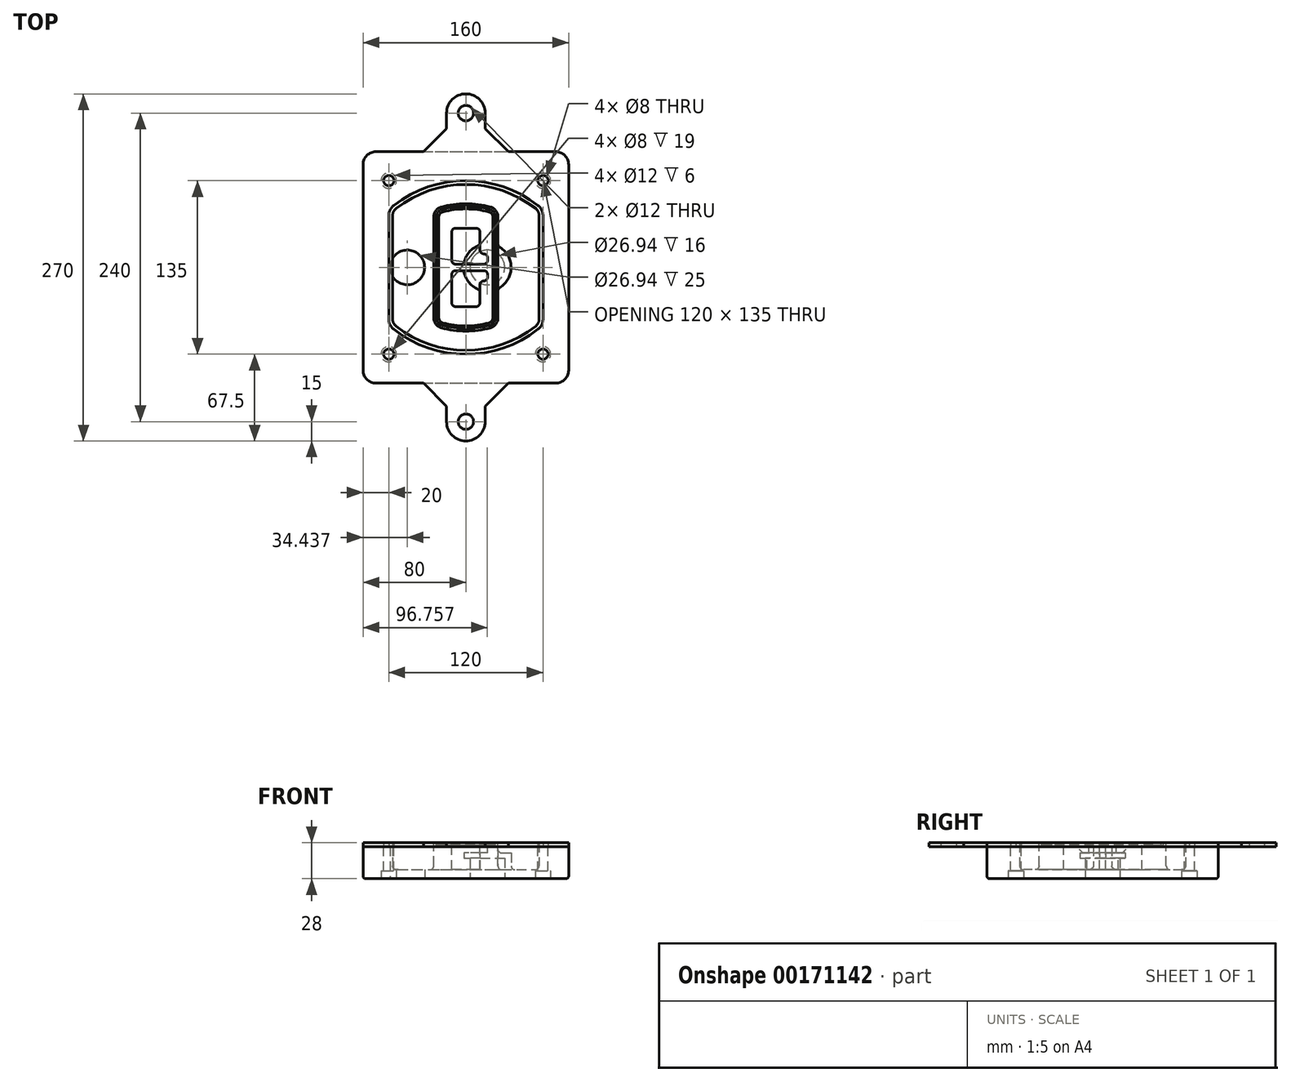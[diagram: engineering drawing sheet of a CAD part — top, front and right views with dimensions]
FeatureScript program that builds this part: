
annotation { "Feature Type Name" : "Feature", "Feature Type Description" : "" }
export const myFeature = defineFeature(function(context is Context, id is Id, definition is map)
    precondition{}
    {
        {
            var Q0;
            Q0=qCreatedBy(makeId("Top.planeOp"),FACE);
            var sketch = newSketch(context, id + "F0", { "sketchPlane" : qUnion([Q0])});
            skPoint(sketch, "E0.rect.middle", {"position": v(0, 0) * mm});
            skLineSegment(sketch, "E1.bottom", {"start": v(-70, -90) * mm, "end": v(70, -90) * mm});
            skLineSegment(sketch, "E1.top", {"start": v(-70, 90) * mm, "end": v(70, 90) * mm});
            skLineSegment(sketch, "E1.left", {"start": v(-80, -80) * mm, "end": v(-80, 80) * mm});
            skLineSegment(sketch, "E1.right", {"start": v(80, -80) * mm, "end": v(80, 80) * mm});
            skLineSegment(sketch, "E2", {"start": v(-80, 90) * mm, "end": v(80, -90) * mm, "construction": true});
            skLineSegment(sketch, "E3", {"start": v(80, 90) * mm, "end": v(-80, -90) * mm, "construction": true});
            skCircle(sketch, "E4", {"center": v(-60, 67.5) * mm, "radius": 4 * mm});
            skCircle(sketch, "E5", {"center": v(60, 67.5) * mm, "radius": 4 * mm});
            skCircle(sketch, "E6", {"center": v(60, -67.5) * mm, "radius": 4 * mm});
            skCircle(sketch, "E7", {"center": v(-60, -67.5) * mm, "radius": 4 * mm});
            skLineSegment(sketch, "E8", {"start": v(-60, 67.5) * mm, "end": v(60, 67.5) * mm, "construction": true});
            skLineSegment(sketch, "E9", {"start": v(60, 67.5) * mm, "end": v(60, -67.5) * mm, "construction": true});
            skLineSegment(sketch, "E10", {"start": v(60, -67.5) * mm, "end": v(-60, -67.5) * mm, "construction": true});
            skLineSegment(sketch, "E11", {"start": v(-60, -67.5) * mm, "end": v(-60, 67.5) * mm, "construction": true});
            skLineSegment(sketch, "E12", {"start": v(-60, 40.3) * mm, "end": v(-60, -40.3) * mm});
            skLineSegment(sketch, "E13", {"start": v(60, 40.3) * mm, "end": v(60, -40.3) * mm});
            skArc(sketch, "E14", {"start": v(56.15, 48.18) * mm, "mid": v(0, 67.5) * mm, "end": v(-56.15, 48.18) * mm});
            skArc(sketch, "E15", {"start": v(-56.15, -48.18) * mm, "mid": v(0, -67.5) * mm, "end": v(56.15, -48.18) * mm});
            skLineSegment(sketch, "E16", {"start": v(-60, 0) * mm, "end": v(60, 0) * mm, "construction": true});
            skPoint(sketch, "E17.visualSharp", {"position": v(-60, -45) * mm});
            skArc(sketch, "E17.filletArc", {"start": v(-60, -40.3) * mm, "mid": v(-58.99, -44.68) * mm, "end": v(-56.15, -48.18) * mm});
            skPoint(sketch, "E18.visualSharp", {"position": v(-60, 45) * mm});
            skArc(sketch, "E18.filletArc", {"start": v(-56.15, 48.18) * mm, "mid": v(-58.99, 44.68) * mm, "end": v(-60, 40.3) * mm});
            skPoint(sketch, "E19.visualSharp", {"position": v(60, 45) * mm});
            skArc(sketch, "E19.filletArc", {"start": v(60, 40.3) * mm, "mid": v(58.99, 44.68) * mm, "end": v(56.15, 48.18) * mm});
            skPoint(sketch, "E20.visualSharp", {"position": v(60, -45) * mm});
            skArc(sketch, "E20.filletArc", {"start": v(56.15, -48.18) * mm, "mid": v(58.99, -44.68) * mm, "end": v(60, -40.3) * mm});
            skPoint(sketch, "E21.visualSharp", {"position": v(-80, 90) * mm});
            skArc(sketch, "E21.filletArc", {"start": v(-70, 90) * mm, "mid": v(-77.07, 87.07) * mm, "end": v(-80, 80) * mm});
            skPoint(sketch, "E22.visualSharp", {"position": v(80, 90) * mm});
            skArc(sketch, "E22.filletArc", {"start": v(80, 80) * mm, "mid": v(77.07, 87.07) * mm, "end": v(70, 90) * mm});
            skPoint(sketch, "E23.visualSharp", {"position": v(80, -90) * mm});
            skArc(sketch, "E23.filletArc", {"start": v(70, -90) * mm, "mid": v(77.07, -87.07) * mm, "end": v(80, -80) * mm});
            skPoint(sketch, "E24.visualSharp", {"position": v(-80, -90) * mm});
            skArc(sketch, "E24.filletArc", {"start": v(-80, -80) * mm, "mid": v(-77.07, -87.07) * mm, "end": v(-70, -90) * mm});
            skArc(sketch, "E25.0", {"start": v(57, 40.3) * mm, "mid": v(56.3, 43.36) * mm, "end": v(54.3, 45.81) * mm});
            skLineSegment(sketch, "E25.1", {"start": v(57, 40.3) * mm, "end": v(57, -40.3) * mm});
            skArc(sketch, "E25.2", {"start": v(54.3, -45.81) * mm, "mid": v(56.3, -43.36) * mm, "end": v(57, -40.3) * mm});
            skArc(sketch, "E25.3", {"start": v(-54.3, -45.81) * mm, "mid": v(0, -64.5) * mm, "end": v(54.3, -45.81) * mm});
            skArc(sketch, "E25.4", {"start": v(-57, -40.3) * mm, "mid": v(-56.3, -43.36) * mm, "end": v(-54.3, -45.81) * mm});
            skArc(sketch, "E25.5", {"start": v(54.3, 45.81) * mm, "mid": v(0, 64.5) * mm, "end": v(-54.3, 45.81) * mm});
            skLineSegment(sketch, "E25.6", {"start": v(-57, 40.3) * mm, "end": v(-57, -40.3) * mm});
            skArc(sketch, "E25.7", {"start": v(-54.3, 45.81) * mm, "mid": v(-56.3, 43.36) * mm, "end": v(-57, 40.3) * mm});
            skArc(sketch, "E26.0", {"start": v(-58.62, 51.33) * mm, "mid": v(-62.58, 46.43) * mm, "end": v(-64, 40.3) * mm});
            skArc(sketch, "E26.1", {"start": v(58.62, 51.33) * mm, "mid": v(0, 71.5) * mm, "end": v(-58.62, 51.33) * mm});
            skArc(sketch, "E26.2", {"start": v(64, 40.3) * mm, "mid": v(62.58, 46.43) * mm, "end": v(58.62, 51.33) * mm});
            skLineSegment(sketch, "E26.3", {"start": v(64, 40.3) * mm, "end": v(64, -40.3) * mm});
            skArc(sketch, "E26.4", {"start": v(58.62, -51.33) * mm, "mid": v(62.58, -46.43) * mm, "end": v(64, -40.3) * mm});
            skLineSegment(sketch, "E26.5", {"start": v(-64, 40.3) * mm, "end": v(-64, -40.3) * mm});
            skArc(sketch, "E26.6", {"start": v(-58.62, -51.33) * mm, "mid": v(0, -71.5) * mm, "end": v(58.62, -51.33) * mm});
            skArc(sketch, "E26.7", {"start": v(-64, -40.3) * mm, "mid": v(-62.58, -46.43) * mm, "end": v(-58.62, -51.33) * mm});
            skSolve(sketch);
        }
        {
            var Q0;
            Q0=makeQuery(id+"F0.imprint","IMPRINT",FACE,{"disambiguationData":[TD([[makeQuery(id+"F0.imprint","IMPRINT",EDGE,{"derivedFrom":sQuery(id+"F0.wireOp",EDGE,"E1.bottom")}),1.0]])]});
            var Q1;
            Q1=makeQuery(id+"F0.imprint","IMPRINT",FACE,{"disambiguationData":[TD([[makeQuery(id+"F0.imprint","IMPRINT",EDGE,{"derivedFrom":sQuery(id+"F0.wireOp",EDGE,"E12")}),1.0]])]});
            var Q2;
            Q2=makeQuery(id+"F0.imprint","IMPRINT",FACE,{"disambiguationData":[TD([[makeQuery(id+"F0.imprint","IMPRINT",EDGE,{"derivedFrom":sQuery(id+"F0.wireOp",EDGE,"E25.0")}),1.0]])]});
            var Q3;
            Q3=makeQuery(id+"F0.imprint","IMPRINT",FACE,{"disambiguationData":[TD([[makeQuery(id+"F0.imprint","IMPRINT",EDGE,{"derivedFrom":sQuery(id+"F0.wireOp",EDGE,"E12")}),-1.0]])]});
            extrude(context, id + "F1", {"entities" : qUnion([Q0, Q1, Q2, Q3]), "oppositeDirection" : true, "depth" : 25 * mm});
        }
        {
            var Q0;
            Q0=makeQuery(id+"F0.imprint","IMPRINT",FACE,{"disambiguationData":[TD([[makeQuery(id+"F0.imprint","IMPRINT",EDGE,{"derivedFrom":sQuery(id+"F0.wireOp",EDGE,"E12")}),1.0]])]});
            extrude(context, id + "F2", {"entities" : qUnion([Q0]), "operationType" : NewBodyOperationType.ADD, "depth" : 3 * mm});
        }
        {
            var Q0;
            Q0=makeQuery(id+"F0.imprint","IMPRINT",FACE,{"disambiguationData":[TD([[makeQuery(id+"F0.imprint","IMPRINT",EDGE,{"derivedFrom":sQuery(id+"F0.wireOp",EDGE,"E25.0")}),1.0]])]});
            extrude(context, id + "F3", {"entities" : qUnion([Q0]), "operationType" : NewBodyOperationType.REMOVE, "oppositeDirection" : true, "depth" : 18 * mm});
        }
        {
            var Q0;
            Q0=makeQuery(id+"F2.opExtrude","CAP_FACE",FACE,{"disambiguationData":[OSD([sQuery(id+"F0.wireOp",EDGE,"E12"),sQuery(id+"F0.wireOp",EDGE,"E13"),sQuery(id+"F0.wireOp",EDGE,"E14"),sQuery(id+"F0.wireOp",EDGE,"E15"),sQuery(id+"F0.wireOp",EDGE,"E17.filletArc"),sQuery(id+"F0.wireOp",EDGE,"E18.filletArc"),sQuery(id+"F0.wireOp",EDGE,"E19.filletArc"),sQuery(id+"F0.wireOp",EDGE,"E20.filletArc"),sQuery(id+"F0.wireOp",EDGE,"E25.0"),sQuery(id+"F0.wireOp",EDGE,"E25.1"),sQuery(id+"F0.wireOp",EDGE,"E25.2"),sQuery(id+"F0.wireOp",EDGE,"E25.3"),sQuery(id+"F0.wireOp",EDGE,"E25.4"),sQuery(id+"F0.wireOp",EDGE,"E25.5"),sQuery(id+"F0.wireOp",EDGE,"E25.6"),sQuery(id+"F0.wireOp",EDGE,"E25.7")])],"isStart":false});
            var sketch = newSketch(context, id + "F4", { "sketchPlane" : qUnion([Q0])});
            skArc(sketch, "E27.0", {"start": v(-19.08, -46.97) * mm, "mid": v(0, -49.5) * mm, "end": v(19.08, -46.97) * mm});
            skArc(sketch, "E28.0", {"start": v(19.08, 46.97) * mm, "mid": v(0, 49.5) * mm, "end": v(-19.08, 46.97) * mm});
            skLineSegment(sketch, "E29", {"start": v(-25, 39.25) * mm, "end": v(-25, -39.25) * mm});
            skLineSegment(sketch, "E30", {"start": v(25, 39.25) * mm, "end": v(25, -39.25) * mm});
            skLineSegment(sketch, "E31", {"start": v(-25, 45.1) * mm, "end": v(25, 45.1) * mm, "construction": true});
            skLineSegment(sketch, "E32", {"start": v(-25, -45.1) * mm, "end": v(25, -45.1) * mm, "construction": true});
            skPoint(sketch, "E33.visualSharp", {"position": v(-25, 45.1) * mm});
            skArc(sketch, "E33.filletArc", {"start": v(-19.08, 46.97) * mm, "mid": v(-23.35, 44.11) * mm, "end": v(-25, 39.25) * mm});
            skPoint(sketch, "E34.visualSharp", {"position": v(25, 45.1) * mm});
            skArc(sketch, "E34.filletArc", {"start": v(25, 39.25) * mm, "mid": v(23.35, 44.11) * mm, "end": v(19.08, 46.97) * mm});
            skPoint(sketch, "E35.visualSharp", {"position": v(25, -45.1) * mm});
            skArc(sketch, "E35.filletArc", {"start": v(19.08, -46.97) * mm, "mid": v(23.35, -44.11) * mm, "end": v(25, -39.25) * mm});
            skPoint(sketch, "E36.visualSharp", {"position": v(-25, -45.1) * mm});
            skArc(sketch, "E36.filletArc", {"start": v(-25, -39.25) * mm, "mid": v(-23.35, -44.11) * mm, "end": v(-19.08, -46.97) * mm});
            skArc(sketch, "E37.0", {"start": v(54.3, 45.81) * mm, "mid": v(0, 64.5) * mm, "end": v(-54.3, 45.81) * mm});
            skArc(sketch, "E37.1", {"start": v(-54.3, 45.81) * mm, "mid": v(-56.3, 43.36) * mm, "end": v(-57, 40.3) * mm});
            skLineSegment(sketch, "E37.2", {"start": v(-57, 40.3) * mm, "end": v(-57, -40.3) * mm});
            skArc(sketch, "E37.3", {"start": v(-57, -40.3) * mm, "mid": v(-56.3, -43.36) * mm, "end": v(-54.3, -45.81) * mm});
            skArc(sketch, "E37.4", {"start": v(-54.3, -45.81) * mm, "mid": v(0, -64.5) * mm, "end": v(54.3, -45.81) * mm});
            skArc(sketch, "E37.5", {"start": v(54.3, -45.81) * mm, "mid": v(56.3, -43.36) * mm, "end": v(57, -40.3) * mm});
            skLineSegment(sketch, "E37.6", {"start": v(57, 40.3) * mm, "end": v(57, -40.3) * mm});
            skArc(sketch, "E37.7", {"start": v(57, 40.3) * mm, "mid": v(56.3, 43.36) * mm, "end": v(54.3, 45.81) * mm});
            skLineSegment(sketch, "E38.0", {"start": v(23, 39.25) * mm, "end": v(23, -39.25) * mm});
            skArc(sketch, "E38.1", {"start": v(18.56, -45.04) * mm, "mid": v(21.76, -42.9) * mm, "end": v(23, -39.25) * mm});
            skArc(sketch, "E38.2", {"start": v(-18.56, -45.04) * mm, "mid": v(0, -47.5) * mm, "end": v(18.56, -45.04) * mm});
            skArc(sketch, "E38.3", {"start": v(-23, -39.25) * mm, "mid": v(-21.76, -42.9) * mm, "end": v(-18.56, -45.04) * mm});
            skLineSegment(sketch, "E38.4", {"start": v(-23, 39.25) * mm, "end": v(-23, -39.25) * mm});
            skArc(sketch, "E38.5", {"start": v(23, 39.25) * mm, "mid": v(21.76, 42.9) * mm, "end": v(18.56, 45.04) * mm});
            skArc(sketch, "E38.6", {"start": v(-18.56, 45.04) * mm, "mid": v(-21.76, 42.9) * mm, "end": v(-23, 39.25) * mm});
            skArc(sketch, "E38.7", {"start": v(18.56, 45.04) * mm, "mid": v(0, 47.5) * mm, "end": v(-18.56, 45.04) * mm});
            skArc(sketch, "E39.0", {"start": v(21, 39.25) * mm, "mid": v(20.18, 41.68) * mm, "end": v(18.04, 43.1) * mm});
            skLineSegment(sketch, "E39.1", {"start": v(21, 39.25) * mm, "end": v(21, -39.25) * mm});
            skArc(sketch, "E39.2", {"start": v(18.04, -43.1) * mm, "mid": v(20.18, -41.68) * mm, "end": v(21, -39.25) * mm});
            skArc(sketch, "E39.3", {"start": v(-18.04, -43.1) * mm, "mid": v(0, -45.5) * mm, "end": v(18.04, -43.1) * mm});
            skArc(sketch, "E39.4", {"start": v(-21, -39.25) * mm, "mid": v(-20.18, -41.68) * mm, "end": v(-18.04, -43.1) * mm});
            skArc(sketch, "E39.5", {"start": v(18.04, 43.1) * mm, "mid": v(0, 45.5) * mm, "end": v(-18.04, 43.1) * mm});
            skLineSegment(sketch, "E39.6", {"start": v(-21, 39.25) * mm, "end": v(-21, -39.25) * mm});
            skArc(sketch, "E39.7", {"start": v(-18.04, 43.1) * mm, "mid": v(-20.18, 41.68) * mm, "end": v(-21, 39.25) * mm});
            skLineSegment(sketch, "E40", {"start": v(-25, 0) * mm, "end": v(25, 0) * mm, "construction": true});
            skLineSegment(sketch, "E41", {"start": v(-11, 5.5) * mm, "end": v(-11, 27.5) * mm});
            skLineSegment(sketch, "E42", {"start": v(-8, 30.5) * mm, "end": v(8, 30.5) * mm});
            skLineSegment(sketch, "E43", {"start": v(11, 27.5) * mm, "end": v(11, 13.5) * mm});
            skLineSegment(sketch, "E44", {"start": v(14, 10.5) * mm, "end": v(14, 10.5) * mm});
            skLineSegment(sketch, "E45", {"start": v(17, 7.5) * mm, "end": v(17, 5.5) * mm});
            skLineSegment(sketch, "E46", {"start": v(14, 2.5) * mm, "end": v(-8, 2.5) * mm});
            skPoint(sketch, "E47.visualSharp", {"position": v(-11, 30.5) * mm});
            skArc(sketch, "E47.filletArc", {"start": v(-8, 30.5) * mm, "mid": v(-10.12, 29.62) * mm, "end": v(-11, 27.5) * mm});
            skPoint(sketch, "E48.visualSharp", {"position": v(11, 30.5) * mm});
            skArc(sketch, "E48.filletArc", {"start": v(11, 27.5) * mm, "mid": v(10.12, 29.62) * mm, "end": v(8, 30.5) * mm});
            skPoint(sketch, "E49.visualSharp", {"position": v(11, 10.5) * mm});
            skArc(sketch, "E49.filletArc", {"start": v(11, 13.5) * mm, "mid": v(11.88, 11.38) * mm, "end": v(14, 10.5) * mm});
            skPoint(sketch, "E50.visualSharp", {"position": v(17, 10.5) * mm});
            skArc(sketch, "E50.filletArc", {"start": v(17, 7.5) * mm, "mid": v(16.12, 9.62) * mm, "end": v(14, 10.5) * mm});
            skPoint(sketch, "E51.visualSharp", {"position": v(17, 2.5) * mm});
            skArc(sketch, "E51.filletArc", {"start": v(14, 2.5) * mm, "mid": v(16.12, 3.38) * mm, "end": v(17, 5.5) * mm});
            skPoint(sketch, "E52.visualSharp", {"position": v(-11, 2.5) * mm});
            skArc(sketch, "E52.filletArc", {"start": v(-11, 5.5) * mm, "mid": v(-10.12, 3.38) * mm, "end": v(-8, 2.5) * mm});
            skLineSegment(sketch, "E53.0.MirrorCS", {"start": v(14, -2.5) * mm, "end": v(-8, -2.5) * mm});
            skArc(sketch, "E54.0.MirrorCS", {"start": v(-11, -5.5) * mm, "mid": v(-10.12, -3.38) * mm, "end": v(-8, -2.5) * mm});
            skLineSegment(sketch, "E55.0.MirrorCS", {"start": v(-11, -5.5) * mm, "end": v(-11, -27.5) * mm});
            skArc(sketch, "E56.0.MirrorCS", {"start": v(-8, -30.5) * mm, "mid": v(-10.12, -29.62) * mm, "end": v(-11, -27.5) * mm});
            skLineSegment(sketch, "E57.0.MirrorCS", {"start": v(-8, -30.5) * mm, "end": v(8, -30.5) * mm});
            skArc(sketch, "E58.0.MirrorCS", {"start": v(11, -27.5) * mm, "mid": v(10.12, -29.62) * mm, "end": v(8, -30.5) * mm});
            skLineSegment(sketch, "E59.0.MirrorCS", {"start": v(11, -27.5) * mm, "end": v(11, -13.5) * mm});
            skArc(sketch, "E60.0.MirrorCS", {"start": v(11, -13.5) * mm, "mid": v(11.88, -11.38) * mm, "end": v(14, -10.5) * mm});
            skArc(sketch, "E61.0.MirrorCS", {"start": v(17, -7.5) * mm, "mid": v(16.12, -9.62) * mm, "end": v(14, -10.5) * mm});
            skLineSegment(sketch, "E62.0.MirrorCS", {"start": v(17, -7.5) * mm, "end": v(17, -5.5) * mm});
            skArc(sketch, "E63.0.MirrorCS", {"start": v(14, -2.5) * mm, "mid": v(16.12, -3.38) * mm, "end": v(17, -5.5) * mm});
            skSolve(sketch);
        }
        {
            var Q0;
            Q0=makeQuery(id+"F4.imprint","IMPRINT",FACE,{"disambiguationData":[TD([[makeQuery(id+"F4.imprint","IMPRINT",EDGE,{"derivedFrom":sQuery(id+"F4.wireOp",EDGE,"E27.0")}),1.0]])]});
            var Q1;
            Q1=makeQuery(id+"F4.imprint","IMPRINT",FACE,{"disambiguationData":[TD([[makeQuery(id+"F4.imprint","IMPRINT",EDGE,{"derivedFrom":sQuery(id+"F4.wireOp",EDGE,"E38.0")}),-1.0]])]});
            var Q2;
            Q2=makeQuery(id+"F4.imprint","IMPRINT",FACE,{"disambiguationData":[TD([[makeQuery(id+"F4.imprint","IMPRINT",EDGE,{"derivedFrom":sQuery(id+"F4.wireOp",EDGE,"E39.0")}),1.0]])]});
            extrude(context, id + "F5", {"entities" : qUnion([Q0, Q1, Q2]), "operationType" : NewBodyOperationType.ADD, "endBound" : BoundingType.UP_TO_NEXT, "oppositeDirection" : true, "depth" : 25 * mm});
        }
        {
            var Q0;
            Q0=makeQuery(id+"F4.imprint","IMPRINT",FACE,{"disambiguationData":[TD([[makeQuery(id+"F4.imprint","IMPRINT",EDGE,{"derivedFrom":sQuery(id+"F4.wireOp",EDGE,"E38.0")}),-1.0]])]});
            extrude(context, id + "F6", {"entities" : qUnion([Q0]), "operationType" : NewBodyOperationType.REMOVE, "oppositeDirection" : true, "depth" : 2 * mm});
        }
        {
            var Q0;
            Q0=makeQuery(id+"F1.opExtrude","CAP_FACE",FACE,{"disambiguationData":[OSD([sQuery(id+"F0.wireOp",EDGE,"E1.bottom"),sQuery(id+"F0.wireOp",EDGE,"E1.top"),sQuery(id+"F0.wireOp",EDGE,"E1.left"),sQuery(id+"F0.wireOp",EDGE,"E1.right"),sQuery(id+"F0.wireOp",EDGE,"E4"),sQuery(id+"F0.wireOp",EDGE,"E5"),sQuery(id+"F0.wireOp",EDGE,"E6"),sQuery(id+"F0.wireOp",EDGE,"E7"),sQuery(id+"F0.wireOp",EDGE,"E21.filletArc"),sQuery(id+"F0.wireOp",EDGE,"E22.filletArc"),sQuery(id+"F0.wireOp",EDGE,"E23.filletArc"),sQuery(id+"F0.wireOp",EDGE,"E24.filletArc")])],"isStart":false});
            var sketch = newSketch(context, id + "F7", { "sketchPlane" : qUnion([Q0])});
            skCircle(sketch, "E64", {"center": v(16.76, 0) * mm, "radius": 13.47 * mm});
            skCircle(sketch, "E65", {"center": v(-45.56, 0) * mm, "radius": 13.47 * mm});
            skLineSegment(sketch, "E66", {"start": v(80, 0) * mm, "end": v(-80, 0) * mm});
            skCircle(sketch, "E67", {"center": v(16.76, 0) * mm, "radius": 18.47 * mm});
            skCircle(sketch, "E68", {"center": v(60, -67.5) * mm, "radius": 6 * mm});
            skCircle(sketch, "E69", {"center": v(-60, -67.5) * mm, "radius": 6 * mm});
            skCircle(sketch, "E70", {"center": v(-60, 67.5) * mm, "radius": 6 * mm});
            skCircle(sketch, "E71", {"center": v(60, 67.5) * mm, "radius": 6 * mm});
            skSolve(sketch);
        }
        {
            var Q0;
            {var subQ1=sQuery(id+"F7.wireOp",EDGE,"E66");var subQ4=sQuery(id+"F7.wireOp",EDGE,"E64");var subQ6=makeQuery(id+"F7.imprint","INTERSECT",VERTEX,{"disambiguationData":[OD(0.0)],"derivedFrom":[subQ4,subQ1]});Q0=makeQuery(id+"F7.imprint","IMPRINT",FACE,{"disambiguationData":[TD([[makeQuery(id+"F7.imprint","IMPRINT",EDGE,{"disambiguationData":[TD([[subQ6,-1.0]])],"derivedFrom":subQ4}),-1.0]])]});}
            var Q1;
            {var subQ0=sQuery(id+"F7.wireOp",EDGE,"E66");var subQ1=sQuery(id+"F7.wireOp",EDGE,"E64");var subQ3=makeQuery(id+"F7.imprint","INTERSECT",VERTEX,{"disambiguationData":[OD(0.0)],"derivedFrom":[subQ1,subQ0]});Q1=makeQuery(id+"F7.imprint","IMPRINT",FACE,{"disambiguationData":[TD([[makeQuery(id+"F7.imprint","IMPRINT",EDGE,{"disambiguationData":[TD([[subQ3,-1.0]])],"derivedFrom":subQ1}),1.0]])]});}
            var Q2;
            {var subQ0=sQuery(id+"F7.wireOp",EDGE,"E66");var subQ1=sQuery(id+"F7.wireOp",EDGE,"E64");var subQ3=makeQuery(id+"F7.imprint","INTERSECT",VERTEX,{"disambiguationData":[OD(0.0)],"derivedFrom":[subQ1,subQ0]});Q2=makeQuery(id+"F7.imprint","IMPRINT",FACE,{"disambiguationData":[TD([[makeQuery(id+"F7.imprint","IMPRINT",EDGE,{"disambiguationData":[TD([[subQ3,1.0]])],"derivedFrom":subQ1}),1.0]])]});}
            var Q3;
            {var subQ1=sQuery(id+"F7.wireOp",EDGE,"E66");var subQ4=sQuery(id+"F7.wireOp",EDGE,"E64");var subQ6=makeQuery(id+"F7.imprint","INTERSECT",VERTEX,{"disambiguationData":[OD(0.0)],"derivedFrom":[subQ4,subQ1]});Q3=makeQuery(id+"F7.imprint","IMPRINT",FACE,{"disambiguationData":[TD([[makeQuery(id+"F7.imprint","IMPRINT",EDGE,{"disambiguationData":[TD([[subQ6,1.0]])],"derivedFrom":subQ4}),-1.0]])]});}
            extrude(context, id + "F8", {"entities" : qUnion([Q0, Q1, Q2, Q3]), "operationType" : NewBodyOperationType.ADD, "oppositeDirection" : true, "depth" : 20 * mm});
        }
        {
            var Q0;
            {var subQ0=sQuery(id+"F7.wireOp",EDGE,"E66");var subQ1=sQuery(id+"F7.wireOp",EDGE,"E64");var subQ3=makeQuery(id+"F7.imprint","INTERSECT",VERTEX,{"disambiguationData":[OD(0.0)],"derivedFrom":[subQ1,subQ0]});Q0=makeQuery(id+"F7.imprint","IMPRINT",FACE,{"disambiguationData":[TD([[makeQuery(id+"F7.imprint","IMPRINT",EDGE,{"disambiguationData":[TD([[subQ3,-1.0]])],"derivedFrom":subQ1}),1.0]])]});}
            var Q1;
            {var subQ0=sQuery(id+"F7.wireOp",EDGE,"E66");var subQ1=sQuery(id+"F7.wireOp",EDGE,"E64");var subQ3=makeQuery(id+"F7.imprint","INTERSECT",VERTEX,{"disambiguationData":[OD(0.0)],"derivedFrom":[subQ1,subQ0]});Q1=makeQuery(id+"F7.imprint","IMPRINT",FACE,{"disambiguationData":[TD([[makeQuery(id+"F7.imprint","IMPRINT",EDGE,{"disambiguationData":[TD([[subQ3,1.0]])],"derivedFrom":subQ1}),1.0]])]});}
            extrude(context, id + "F9", {"entities" : qUnion([Q0, Q1]), "operationType" : NewBodyOperationType.REMOVE, "oppositeDirection" : true, "depth" : 16 * mm});
        }
        {
            var Q0;
            {var subQ0=sQuery(id+"F7.wireOp",EDGE,"E66");var subQ1=sQuery(id+"F7.wireOp",EDGE,"E65");var subQ3=makeQuery(id+"F7.imprint","INTERSECT",VERTEX,{"disambiguationData":[OD(0.0)],"derivedFrom":[subQ1,subQ0]});Q0=makeQuery(id+"F7.imprint","IMPRINT",FACE,{"disambiguationData":[TD([[makeQuery(id+"F7.imprint","IMPRINT",EDGE,{"disambiguationData":[TD([[subQ3,-1.0]])],"derivedFrom":subQ1}),1.0]])]});}
            var Q1;
            {var subQ0=sQuery(id+"F7.wireOp",EDGE,"E66");var subQ1=sQuery(id+"F7.wireOp",EDGE,"E65");var subQ3=makeQuery(id+"F7.imprint","INTERSECT",VERTEX,{"disambiguationData":[OD(0.0)],"derivedFrom":[subQ1,subQ0]});Q1=makeQuery(id+"F7.imprint","IMPRINT",FACE,{"disambiguationData":[TD([[makeQuery(id+"F7.imprint","IMPRINT",EDGE,{"disambiguationData":[TD([[subQ3,1.0]])],"derivedFrom":subQ1}),1.0]])]});}
            extrude(context, id + "F10", {"entities" : qUnion([Q0, Q1]), "operationType" : NewBodyOperationType.REMOVE, "oppositeDirection" : true, "depth" : 25 * mm});
        }
        {
            var Q0;
            Q0=makeQuery(id+"F7.imprint","IMPRINT",FACE,{"disambiguationData":[TD([[makeQuery(id+"F7.imprint","IMPRINT",EDGE,{"derivedFrom":sQuery(id+"F7.wireOp",EDGE,"E68")}),1.0]])]});
            var Q1;
            Q1=makeQuery(id+"F7.imprint","IMPRINT",FACE,{"disambiguationData":[TD([[makeQuery(id+"F7.imprint","IMPRINT",EDGE,{"derivedFrom":makeQuery(id+"F1.opExtrude","CAP_EDGE",EDGE,{"disambiguationData":[OSD([sQuery(id+"F0.wireOp",EDGE,"E5")])],"isStart":false})}),-1.0]])]});
            var Q2;
            Q2=makeQuery(id+"F7.imprint","IMPRINT",FACE,{"disambiguationData":[TD([[makeQuery(id+"F7.imprint","IMPRINT",EDGE,{"derivedFrom":sQuery(id+"F7.wireOp",EDGE,"E69")}),1.0]])]});
            var Q3;
            Q3=makeQuery(id+"F7.imprint","IMPRINT",FACE,{"disambiguationData":[TD([[makeQuery(id+"F7.imprint","IMPRINT",EDGE,{"derivedFrom":makeQuery(id+"F1.opExtrude","CAP_EDGE",EDGE,{"disambiguationData":[OSD([sQuery(id+"F0.wireOp",EDGE,"E4")])],"isStart":false})}),-1.0]])]});
            var Q4;
            Q4=makeQuery(id+"F7.imprint","IMPRINT",FACE,{"disambiguationData":[TD([[makeQuery(id+"F7.imprint","IMPRINT",EDGE,{"derivedFrom":sQuery(id+"F7.wireOp",EDGE,"E70")}),1.0]])]});
            var Q5;
            Q5=makeQuery(id+"F7.imprint","IMPRINT",FACE,{"disambiguationData":[TD([[makeQuery(id+"F7.imprint","IMPRINT",EDGE,{"derivedFrom":makeQuery(id+"F1.opExtrude","CAP_EDGE",EDGE,{"disambiguationData":[OSD([sQuery(id+"F0.wireOp",EDGE,"E7")])],"isStart":false})}),-1.0]])]});
            var Q6;
            Q6=makeQuery(id+"F7.imprint","IMPRINT",FACE,{"disambiguationData":[TD([[makeQuery(id+"F7.imprint","IMPRINT",EDGE,{"derivedFrom":sQuery(id+"F7.wireOp",EDGE,"E71")}),1.0]])]});
            var Q7;
            Q7=makeQuery(id+"F7.imprint","IMPRINT",FACE,{"disambiguationData":[TD([[makeQuery(id+"F7.imprint","IMPRINT",EDGE,{"derivedFrom":makeQuery(id+"F1.opExtrude","CAP_EDGE",EDGE,{"disambiguationData":[OSD([sQuery(id+"F0.wireOp",EDGE,"E6")])],"isStart":false})}),-1.0]])]});
            extrude(context, id + "F11", {"entities" : qUnion([Q0, Q1, Q2, Q3, Q4, Q5, Q6, Q7]), "operationType" : NewBodyOperationType.REMOVE, "oppositeDirection" : true, "depth" : 6 * mm});
        }
        {
            var Q0;
            Q0=makeQuery(id+"F9.boolean.opBoolean","COPY",FACE,{"derivedFrom":makeQuery(id+"F9.opExtrude","CAP_FACE",FACE,{"disambiguationData":[OSD([sQuery(id+"F7.wireOp",EDGE,"E64")])],"isStart":false})});
            var sketch = newSketch(context, id + "F12", { "sketchPlane" : qUnion([Q0])});
            skArc(sketch, "E72.0", {"start": v(11, 17.55) * mm, "mid": v(2.57, 11.82) * mm, "end": v(-1.54, 2.5) * mm});
            skArc(sketch, "E72.1", {"start": v(-1.54, -2.5) * mm, "mid": v(2.57, -11.82) * mm, "end": v(11, -17.55) * mm});
            skLineSegment(sketch, "E73", {"start": v(-1.54, -2.5) * mm, "end": v(14, -2.5) * mm});
            skLineSegment(sketch, "E74.0", {"start": v(14, 2.5) * mm, "end": v(-1.54, 2.5) * mm});
            skArc(sketch, "E74.1", {"start": v(14, 2.5) * mm, "mid": v(16.12, 3.38) * mm, "end": v(17, 5.5) * mm});
            skLineSegment(sketch, "E74.2", {"start": v(17, 7.5) * mm, "end": v(17, 5.5) * mm});
            skArc(sketch, "E74.3", {"start": v(17, 7.5) * mm, "mid": v(16.12, 9.62) * mm, "end": v(14, 10.5) * mm});
            skArc(sketch, "E74.4", {"start": v(11, 13.5) * mm, "mid": v(11.88, 11.38) * mm, "end": v(14, 10.5) * mm});
            skLineSegment(sketch, "E74.5", {"start": v(11, 17.55) * mm, "end": v(11, 13.5) * mm});
            skLineSegment(sketch, "E74.7", {"start": v(14, -2.5) * mm, "end": v(-1.54, -2.5) * mm});
            skArc(sketch, "E74.8", {"start": v(14, -2.5) * mm, "mid": v(16.12, -3.38) * mm, "end": v(17, -5.5) * mm});
            skLineSegment(sketch, "E74.9", {"start": v(17, -7.5) * mm, "end": v(17, -5.5) * mm});
            skArc(sketch, "E74.10", {"start": v(17, -7.5) * mm, "mid": v(16.12, -9.62) * mm, "end": v(14, -10.5) * mm});
            skArc(sketch, "E74.11", {"start": v(11, -13.5) * mm, "mid": v(11.88, -11.38) * mm, "end": v(14, -10.5) * mm});
            skLineSegment(sketch, "E74.12", {"start": v(11, -17.55) * mm, "end": v(11, -13.5) * mm});
            skPoint(sketch, "E75.orphan", {"position": v(11, -27.5) * mm});
            skPoint(sketch, "E76.orphan", {"position": v(-8, -2.5) * mm});
            skPoint(sketch, "E77.orphan", {"position": v(-8, 2.5) * mm});
            skPoint(sketch, "E78.orphan", {"position": v(11, 27.5) * mm});
            skSolve(sketch);
        }
        {
            var Q0;
            {var subQ7=sQuery(id+"F12.wireOp",EDGE,"E72.0");var subQ14=sQuery(id+"F12.wireOp",EDGE,"E72.1");var subQ16=sQuery(id+"F12.wireOp",EDGE,"E74.1");var subQ18=sQuery(id+"F12.wireOp",EDGE,"E74.8");Q0=qUnion([makeQuery(id+"F12.imprint","IMPRINT",FACE,{"disambiguationData":[TD([[makeQuery(id+"F12.imprint","IMPRINT",EDGE,{"derivedFrom":subQ7}),1.0]])]}),makeQuery(id+"F12.imprint","IMPRINT",FACE,{"disambiguationData":[TD([[makeQuery(id+"F12.imprint","IMPRINT",EDGE,{"derivedFrom":subQ14}),1.0]])]}),makeQuery(id+"F12.imprint","IMPRINT",FACE,{"disambiguationData":[TD([[makeQuery(id+"F12.imprint","IMPRINT",EDGE,{"derivedFrom":subQ16}),1.0]])]}),makeQuery(id+"F12.imprint","IMPRINT",FACE,{"disambiguationData":[TD([[makeQuery(id+"F12.imprint","IMPRINT",EDGE,{"derivedFrom":subQ18}),-1.0]])]})]);}
            var Q1;
            Q1=makeQuery(id+"F5.boolean.opBoolean","SPLIT",FACE,{"disambiguationData":[TD([makeQuery(id+"F5.opExtrude","SWEPT_FACE",FACE,{"disambiguationData":[OSD([sQuery(id+"F4.wireOp",EDGE,"E41")])]})])],"derivedFrom":makeQuery(id+"F3.boolean.opBoolean","COPY",FACE,{"derivedFrom":makeQuery(id+"F3.opExtrude","CAP_FACE",FACE,{"disambiguationData":[OSD([sQuery(id+"F0.wireOp",EDGE,"E25.0"),sQuery(id+"F0.wireOp",EDGE,"E25.1"),sQuery(id+"F0.wireOp",EDGE,"E25.2"),sQuery(id+"F0.wireOp",EDGE,"E25.3"),sQuery(id+"F0.wireOp",EDGE,"E25.4"),sQuery(id+"F0.wireOp",EDGE,"E25.5"),sQuery(id+"F0.wireOp",EDGE,"E25.6"),sQuery(id+"F0.wireOp",EDGE,"E25.7")])],"isStart":false})})});
            extrude(context, id + "F13", {"entities" : qUnion([Q0]), "operationType" : NewBodyOperationType.REMOVE, "endBound" : BoundingType.UP_TO_SURFACE, "endBoundEntityFace" : qUnion([Q1]), "depth" : 25 * mm});
        }
        {
            var Q0;
            Q0=makeQuery(id+"F3.boolean.opBoolean","COPY",EDGE,{"derivedFrom":makeQuery(id+"F3.opExtrude","CAP_EDGE",EDGE,{"disambiguationData":[OSD([sQuery(id+"F0.wireOp",EDGE,"E25.6")])],"isStart":false})});
            var Q1;
            Q1=makeQuery(id+"F8.boolean.opBoolean","INTERSECT",EDGE,{"derivedFrom":[makeQuery(id+"F5.opExtrude","SWEPT_FACE",FACE,{"disambiguationData":[OSD([sQuery(id+"F4.wireOp",EDGE,"E30")])]}),makeQuery(id+"F8.opExtrude","CAP_FACE",FACE,{"disambiguationData":[OSD([sQuery(id+"F7.wireOp",EDGE,"E67")])],"isStart":false})]});
            var Q2;
            Q2=makeQuery(id+"F8.boolean.opBoolean","INTERSECT",EDGE,{"disambiguationData":[OD(1.0)],"derivedFrom":[makeQuery(id+"F5.opExtrude","SWEPT_FACE",FACE,{"disambiguationData":[OSD([sQuery(id+"F4.wireOp",EDGE,"E30")])]}),makeQuery(id+"F8.opExtrude","SWEPT_FACE",FACE,{"disambiguationData":[OSD([sQuery(id+"F7.wireOp",EDGE,"E67")])]})]});
            var Q3;
            {var subQ0=sQuery(id+"F4.wireOp",EDGE,"E30");Q3=makeQuery(id+"F8.boolean.opBoolean","SPLIT",EDGE,{"disambiguationData":[TD([makeQuery(id+"F5.opExtrude","SWEPT_FACE",FACE,{"disambiguationData":[OSD([sQuery(id+"F4.wireOp",EDGE,"E35.filletArc")])]})])],"derivedFrom":makeQuery(id+"F5.opExtrude","CAP_EDGE",EDGE,{"disambiguationData":[OSD([subQ0])],"isStart":false})});}
            var Q4;
            {var subQ0=sQuery(id+"F0.wireOp",EDGE,"E25.7");var subQ1=sQuery(id+"F0.wireOp",EDGE,"E25.1");var subQ2=sQuery(id+"F0.wireOp",EDGE,"E25.6");var subQ3=sQuery(id+"F0.wireOp",EDGE,"E25.5");var subQ4=sQuery(id+"F0.wireOp",EDGE,"E25.4");var subQ5=sQuery(id+"F0.wireOp",EDGE,"E25.0");var subQ6=sQuery(id+"F0.wireOp",EDGE,"E25.2");var subQ7=sQuery(id+"F0.wireOp",EDGE,"E25.3");Q4=makeQuery(id+"F8.boolean.opBoolean","INTERSECT",EDGE,{"derivedFrom":[makeQuery(id+"F5.boolean.opBoolean","SPLIT",FACE,{"disambiguationData":[TD([makeQuery(id+"F2.opExtrude","SWEPT_FACE",FACE,{"disambiguationData":[OSD([subQ5])]})])],"derivedFrom":makeQuery(id+"F3.boolean.opBoolean","COPY",FACE,{"derivedFrom":makeQuery(id+"F3.opExtrude","CAP_FACE",FACE,{"disambiguationData":[OSD([subQ5,subQ1,subQ6,subQ7,subQ4,subQ3,subQ2,subQ0])],"isStart":false})})}),makeQuery(id+"F8.opExtrude","SWEPT_FACE",FACE,{"disambiguationData":[OSD([sQuery(id+"F7.wireOp",EDGE,"E67")])]})]});}
            var Q5;
            Q5=makeQuery(id+"F8.boolean.opBoolean","INTERSECT",EDGE,{"disambiguationData":[OD(0.0)],"derivedFrom":[makeQuery(id+"F5.opExtrude","SWEPT_FACE",FACE,{"disambiguationData":[OSD([sQuery(id+"F4.wireOp",EDGE,"E30")])]}),makeQuery(id+"F8.opExtrude","SWEPT_FACE",FACE,{"disambiguationData":[OSD([sQuery(id+"F7.wireOp",EDGE,"E67")])]})]});
            fillet(context, id + "F14", {"entities" : qUnion([Q0, Q1, Q2, Q3, Q4, Q5]), "radius" : 3 * mm, "tangentPropagation" : true, "allowEdgeOverflow" : false});
        }
        {
            var Q0;
            Q0=makeQuery(id+"F1.opExtrude","CAP_EDGE",EDGE,{"disambiguationData":[OSD([sQuery(id+"F0.wireOp",EDGE,"E1.bottom")])],"isStart":false});
            fillet(context, id + "F15", {"entities" : qUnion([Q0]), "radius" : 2 * mm, "tangentPropagation" : true, "allowEdgeOverflow" : false});
        }
        {
            var Q0;
            {var subQ0=sQuery(id+"F0.wireOp",EDGE,"E22.filletArc");var subQ1=sQuery(id+"F0.wireOp",EDGE,"E7");var subQ2=sQuery(id+"F0.wireOp",EDGE,"E6");var subQ3=sQuery(id+"F0.wireOp",EDGE,"E5");var subQ4=sQuery(id+"F0.wireOp",EDGE,"E4");var subQ5=sQuery(id+"F0.wireOp",EDGE,"E1.bottom");var subQ6=sQuery(id+"F0.wireOp",EDGE,"E21.filletArc");var subQ7=sQuery(id+"F0.wireOp",EDGE,"E1.top");var subQ8=sQuery(id+"F0.wireOp",EDGE,"E1.left");var subQ9=sQuery(id+"F0.wireOp",EDGE,"E1.right");var subQ10=sQuery(id+"F0.wireOp",EDGE,"E23.filletArc");var subQ11=sQuery(id+"F0.wireOp",EDGE,"E24.filletArc");Q0=makeQuery(id+"F2.boolean.opBoolean","SPLIT",FACE,{"disambiguationData":[TD([makeQuery(id+"F1.opExtrude","SWEPT_FACE",FACE,{"disambiguationData":[OSD([subQ5])]})])],"derivedFrom":makeQuery(id+"F1.opExtrude","CAP_FACE",FACE,{"disambiguationData":[OSD([subQ5,subQ7,subQ8,subQ9,subQ4,subQ3,subQ2,subQ1,subQ6,subQ0,subQ10,subQ11])],"isStart":true})});}
            var sketch = newSketch(context, id + "F16", { "sketchPlane" : qUnion([Q0])});
            skLineSegment(sketch, "E79", {"start": v(0, 90) * mm, "end": v(0, 120) * mm, "construction": true});
            skCircle(sketch, "E80", {"center": v(0, 120) * mm, "radius": 6 * mm});
            skLineSegment(sketch, "E81", {"start": v(-33, 90) * mm, "end": v(-15, 108) * mm});
            skLineSegment(sketch, "E82", {"start": v(-15, 108) * mm, "end": v(-15, 120) * mm});
            skLineSegment(sketch, "E83", {"start": v(33, 90) * mm, "end": v(15, 108) * mm});
            skLineSegment(sketch, "E84", {"start": v(15, 108) * mm, "end": v(15, 120) * mm});
            skArc(sketch, "E85", {"start": v(15, 120) * mm, "mid": v(0, 135) * mm, "end": v(-15, 120) * mm});
            skLineSegment(sketch, "E86", {"start": v(-80, 0) * mm, "end": v(80, 0) * mm, "construction": true});
            skLineSegment(sketch, "E87.MirrorCS", {"start": v(-33, -90) * mm, "end": v(-15, -108) * mm});
            skLineSegment(sketch, "E88.MirrorCS", {"start": v(-15, -108) * mm, "end": v(-15, -120) * mm});
            skArc(sketch, "E89.MirrorCS", {"start": v(15, -120) * mm, "mid": v(0, -135) * mm, "end": v(-15, -120) * mm});
            skCircle(sketch, "E90.MirrorC", {"center": v(0, -120) * mm, "radius": 6 * mm});
            skLineSegment(sketch, "E91.MirrorCS", {"start": v(15, -108) * mm, "end": v(15, -120) * mm});
            skLineSegment(sketch, "E92.MirrorCS", {"start": v(0, -90) * mm, "end": v(0, -120) * mm, "construction": true});
            skLineSegment(sketch, "E93.MirrorCS", {"start": v(33, -90) * mm, "end": v(15, -108) * mm});
            skSolve(sketch);
        }
        {
            var Q0;
            Q0=makeQuery(id+"F16.imprint","IMPRINT",FACE,{"disambiguationData":[TD([[makeQuery(id+"F16.imprint","IMPRINT",EDGE,{"derivedFrom":sQuery(id+"F16.wireOp",EDGE,"E80")}),-1.0]])]});
            var Q1;
            {var subQ0=sQuery(id+"F16.wireOp",EDGE,"E87.MirrorCS");Q1=makeQuery(id+"F16.imprint","IMPRINT",FACE,{"disambiguationData":[TD([[makeQuery(id+"F16.imprint","IMPRINT",EDGE,{"derivedFrom":subQ0}),1.0]])]});}
            var Q2;
            Q2=makeQuery(id+"F16.imprint","IMPRINT",FACE,{"disambiguationData":[TD([[makeQuery(id+"F16.imprint","IMPRINT",EDGE,{"derivedFrom":makeQuery(id+"F1.opExtrude","CAP_EDGE",EDGE,{"disambiguationData":[OSD([sQuery(id+"F0.wireOp",EDGE,"E1.left")])],"isStart":true})}),-1.0]])]});
            var Q3;
            Q3=makeQuery(id+"F2.opExtrude","CAP_FACE",FACE,{"disambiguationData":[OSD([sQuery(id+"F0.wireOp",EDGE,"E12"),sQuery(id+"F0.wireOp",EDGE,"E13"),sQuery(id+"F0.wireOp",EDGE,"E14"),sQuery(id+"F0.wireOp",EDGE,"E15"),sQuery(id+"F0.wireOp",EDGE,"E17.filletArc"),sQuery(id+"F0.wireOp",EDGE,"E18.filletArc"),sQuery(id+"F0.wireOp",EDGE,"E19.filletArc"),sQuery(id+"F0.wireOp",EDGE,"E20.filletArc"),sQuery(id+"F0.wireOp",EDGE,"E25.0"),sQuery(id+"F0.wireOp",EDGE,"E25.1"),sQuery(id+"F0.wireOp",EDGE,"E25.2"),sQuery(id+"F0.wireOp",EDGE,"E25.3"),sQuery(id+"F0.wireOp",EDGE,"E25.4"),sQuery(id+"F0.wireOp",EDGE,"E25.5"),sQuery(id+"F0.wireOp",EDGE,"E25.6"),sQuery(id+"F0.wireOp",EDGE,"E25.7")])],"isStart":false});
            extrude(context, id + "F17", {"entities" : qUnion([Q0, Q1, Q2]), "endBound" : BoundingType.UP_TO_SURFACE, "endBoundEntityFace" : qUnion([Q3]), "depth" : 25 * mm});
        }
    });
